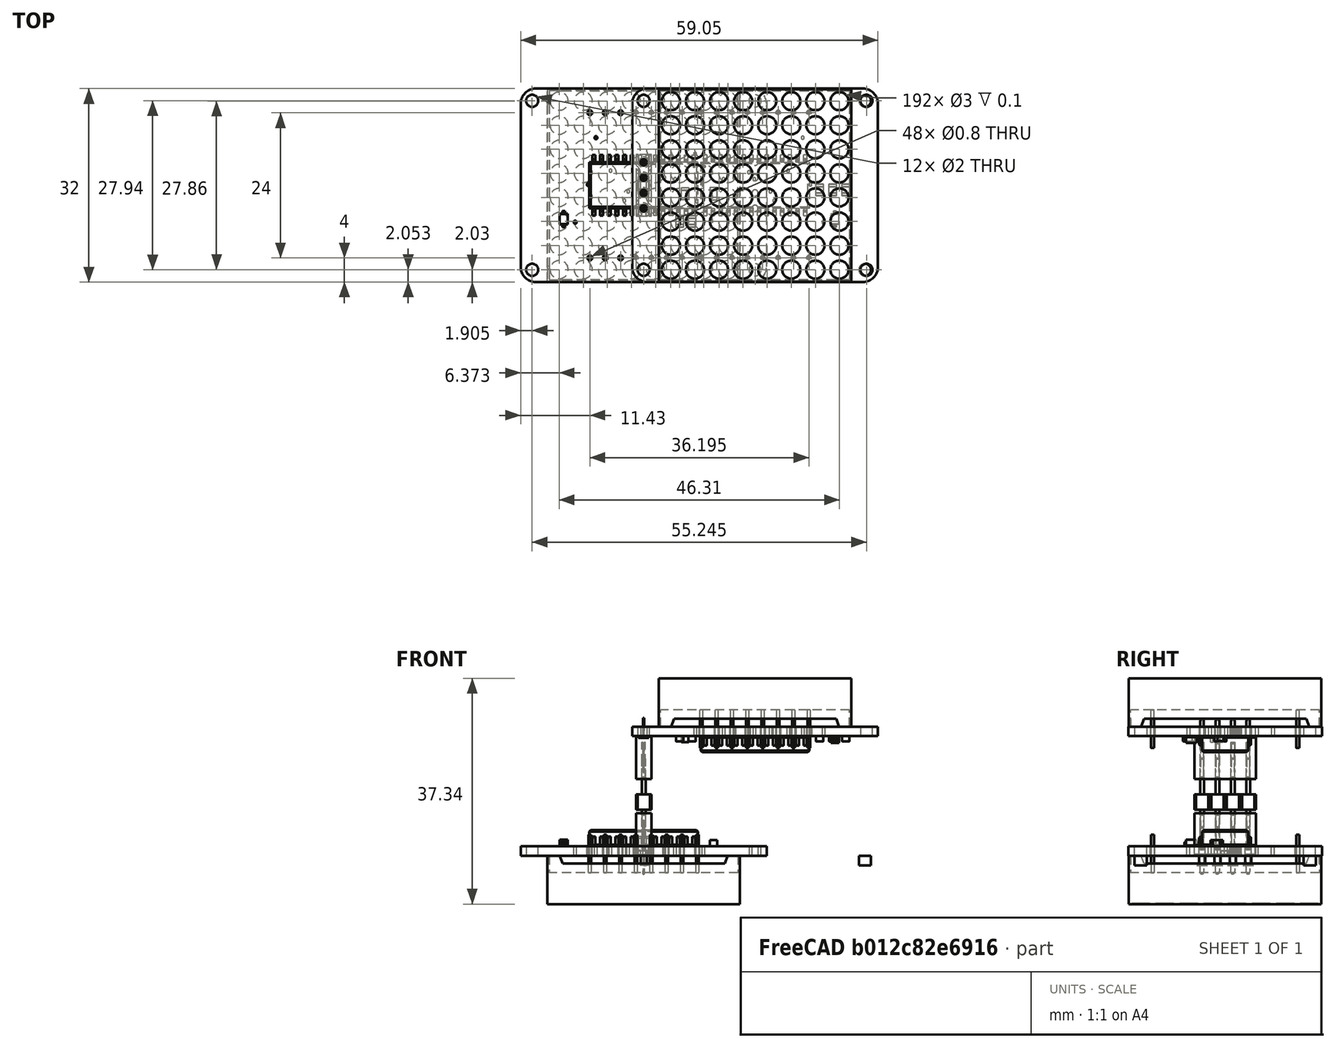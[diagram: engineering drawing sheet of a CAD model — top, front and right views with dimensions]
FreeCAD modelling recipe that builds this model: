
FCSTD DOCUMENT  (FreeCAD 2022.709R28846 (Git))
Label: footprint_LED_matrix_8x8_socket_v2
License: Other
objects: Part::Feature×33, Part::Compound×4, App::Link×4, App::Part×2, Path::FeatureArea×1, Part::Extrusion×1, App::DocumentObjectGroup×1, Part::Compound2×1, Part::MultiFuse×1
note: 41 computed .brp shape members not serialized (recipe doc carries the construction recipe); baked Part::Feature solids carry a one-line shape summary decoded from their .brp

FEATURE [Part::Feature] holes_wire  label="holes_wire#F.Cu#0"
  TreeRank = 3
  shape: bbox 38.08 x 29.94 x 2e-07 mm, 0 faces, 0 solids (baked)
FEATURE [Path::FeatureArea] holes_area  label="holes_area#F.Cu#0"
  Accuracy = 0.0005
  Angle = 45
  AngleShift = 0
  CleanDistance = 0
  ClipFill = 0
  ClipperScale = 10000000
  Coplanar = 0
  Deflection = 0.01
  EndType = 0
  Explode = false
  ExtraPass = 0
  Fill = 1
  FitArcs = true
  FromCenter = false
  JoinType = 0
  LastStepover = 0
  MaxArcPoints = 100
  MinArcPoints = 4
  MiterLimit = 2
  OpenMode = 0
  Operation = 0
  Outline = false
  PocketExtraOffset = 0
  PocketLastStepover = 0
  PocketMaxOffset = 0
  PocketMode = 0
  PocketStepover = 0
  Project = false
  Reorient = false
  RoundPrecision = 0
  SectionCount = 0
  SectionMode = 2
  SectionOffset = 0
  SectionTolerance = 1e-06
  Shift = 0
  Simplify = false
  Sources = -> [holes_wire]
  Stepdown = 1
  Stepover = 0
  SubjectFill = 0
  Thicken = false
  Tolerance = 1e-07
  ToolRadius = 1
  TreeRank = 4
  Unit = 1
FEATURE [Part::Extrusion] holes_solid  label="holes_solid#F.Cu"
  Base = -> holes_area
  Dir = (0,0,1.6)
  DirMode = 0
  FaceMakerClass = Part::FaceMakerBullseye
  InnerTaperAngle = 0
  InnerTaperAngleRev = 0
  LengthFwd = 0
  LengthRev = 0
  Linearize = true
  Placement = pos=(0,0,-1.6) rot=(0,0,1;0rad)
  Solid = false
  Symmetric = false
  TreeRank = 5
FEATURE [Part::Feature] anr_  label="drill_000"
  TreeRank = 37
  shape: bbox 2.02 x 2.02 x 1.6 mm, 4 faces (baked)
FEATURE [Part::Feature] anr_001  label="drill_001"
  TreeRank = 38
  shape: bbox 2.02 x 2.02 x 1.6 mm, 4 faces (baked)
FEATURE [Part::Feature] anr_002  label="drill_002"
  TreeRank = 39
  shape: bbox 1.02 x 1.02 x 1.6 mm, 4 faces (baked)
FEATURE [Part::Feature] anr_003  label="drill_003"
  TreeRank = 40
  shape: bbox 1.02 x 1.02 x 1.6 mm, 4 faces (baked)
FEATURE [Part::Feature] anr_004  label="drill_004"
  TreeRank = 41
  shape: bbox 1.02 x 1.02 x 1.6 mm, 4 faces (baked)
FEATURE [Part::Feature] anr_005  label="drill_005"
  TreeRank = 42
  shape: bbox 1.02 x 1.02 x 1.6 mm, 4 faces (baked)
FEATURE [Part::Compound] annulars  label="TH-Drills"
  Links = -> [anr_,anr_001,anr_002,anr_003,anr_004,anr_005]
  TreeRank = 43
FEATURE [Part::Feature] Shape001  label="topPads"
  Placement = pos=(0,0,-0.01) rot=(0,0,1;0rad)
  TreeRank = 52
  shape: bbox 1.8 x 9.42 x 0.01 mm, 20 faces, 4 solids (baked)
FEATURE [Part::Feature] Shape002  label="btmPads"
  Placement = pos=(0,0,-1.6) rot=(0,0,1;0rad)
  TreeRank = 58
  shape: bbox 1.8 x 9.42 x 0.01 mm, 20 faces, 4 solids (baked)
FEATURE [App::DocumentObjectGroup] Group  label=""LED_8x8_Bi_Color"-fp"
  ClaimAllChildren = true
  ExportMode = 1
  Group = -> [Shape001,Shape002,annulars]
  TreeRank = 59
  _GroupVersion = 1
FEATURE [Part::Feature] Solid  label="PinSocket_1x04_P254mm_Vertical"
  Placement = pos=(0,3.81,0) rot=(0,0,1;0rad)
  TreeRank = 60
  shape: bbox 2.54 x 10.16 x 10.1 mm, 134 faces (baked)
FEATURE [Part::Feature] Solid001  label="PinSocket_1x04_P254mm_Vertical001"
  Placement = pos=(0,-3.81,19.685) rot=(1,0,0;3.14159rad)
  TreeRank = 61
  shape: bbox 2.54 x 10.16 x 10.1 mm, 134 faces (baked)
FEATURE [Part::Feature] Solid002  label="PinHeader_1x04_P254mm_Vertical"
  Placement = pos=(0,3.81,7.62) rot=(0,0,1;0rad)
  TreeRank = 62
  shape: bbox 2.54 x 10.16 x 11.54 mm, 100 faces (baked)
FEATURE [Part::Feature] Solid003  label="Board"
  TreeRank = 65
  shape: bbox 40.64 x 32 x 1.57 mm, 45 faces (baked)
FEATURE [Part::Feature] Solid004  label="SEGMENT_BL-M12A881UR"
  Placement = pos=(0,0,0) rot=(0,1,0;3.14159rad)
  TreeRank = 66
  shape: bbox 31.8 x 31.8 x 11.5 mm, 186 faces (baked)
FEATURE [Part::Feature] Solid005
  TreeRank = 71
  shape: bbox 1.94 x 1.19 x 0.79 mm, 6 faces (baked)
FEATURE [Part::Feature] Solid006
  TreeRank = 72
  shape: bbox 0.5 x 1.25 x 0.85 mm, 30 faces (baked)
FEATURE [Part::Feature] Solid007
  TreeRank = 73
  shape: bbox 0.5 x 1.25 x 0.85 mm, 30 faces (baked)
FEATURE [Part::Compound2] Compound  label="R0805"
  Links = -> [Solid005,Solid006,Solid007]
  Placement = pos=(10.414,-5.969,1.57) rot=(0,0,-1;1.5708rad)
  TreeRank = 74
FEATURE [App::Link] Link  label="R0805:R2"
  AutoLinkLabel = true
  AutoPlacement = true
  LinkPlacement = pos=(12.446,-5.969,1.57) rot=(0,0,-1;1.5708rad)
  LinkedObject = -> Compound
  Placement = pos=(12.446,-5.969,1.57) rot=(0,0,-1;1.5708rad)
  ShowElement = false
  SyncGroupVisibility = false
  TreeRank = 86
  _LinkVersion = 1
FEATURE [App::Link] Link001  label="R0805:R3"
  AutoLinkLabel = true
  AutoPlacement = true
  LinkPlacement = pos=(-12.827,-0.762,1.57) rot=(0,0,1;1.5708rad)
  LinkedObject = -> Compound
  Placement = pos=(-12.827,-0.762,1.57) rot=(0,0,1;1.5708rad)
  ShowElement = false
  SyncGroupVisibility = false
  TreeRank = 87
  _LinkVersion = 1
FEATURE [App::Link] Link002  label="R0805:R4"
  AutoLinkLabel = true
  AutoPlacement = true
  LinkPlacement = pos=(-10.668,-0.762,1.57) rot=(0,0,1;1.5708rad)
  LinkedObject = -> Compound
  Placement = pos=(-10.668,-0.762,1.57) rot=(0,0,1;1.5708rad)
  ShowElement = false
  SyncGroupVisibility = false
  TreeRank = 88
  _LinkVersion = 1
FEATURE [App::Link] Link003  label="R0805:R5"
  AutoLinkLabel = true
  AutoPlacement = true
  LinkPlacement = pos=(-14.986,-0.762,1.57) rot=(0,0,1;1.5708rad)
  LinkedObject = -> Compound
  Placement = pos=(-14.986,-0.762,1.57) rot=(0,0,1;1.5708rad)
  ShowElement = false
  SyncGroupVisibility = false
  TreeRank = 89
  _LinkVersion = 1
FEATURE [Part::Feature] Solid008  label="SOD-323F"
  Placement = pos=(-13.208,-5.588,1.57) rot=(0,0,1;1.5708rad)
  TreeRank = 90
  shape: bbox 1.35 x 2.7 x 1.1 mm, 38 faces (baked)
FEATURE [Part::Feature] Solid009  label="C0805"
  Placement = pos=(11.557,-1.397,1.57) rot=(0,0,1;1.5708rad)
  TreeRank = 91
  shape: bbox 1.25 x 2 x 1 mm, 14 faces (baked)
FEATURE [Part::Feature] Solid010  label="SOP28_300MIL"
  Placement = pos=(0,0,1.57) rot=(0,0,1;3.14159rad)
  TreeRank = 92
  shape: bbox 18 x 10 x 2.65 mm, 376 faces (baked)
FEATURE [App::Part] Part  label="PCB Component"
  ClaimAllChildren = false
  ExportMode = 1
  Group = -> [Solid003,Solid004,Compound,Link,Link001,Link002,Link003,Solid008,Solid009,Solid010,Solid005,Solid006,Solid007]
  Origin = -> Origin
  TreeRank = 94
  _ExportChildren = -> [Solid003,Solid004,Compound,Link,Link001,Link002,Link003,Solid008,Solid009,Solid010]
  _GroupVersion = 1
FEATURE [App::Part] Part001  label="Adafruit 1.2inch 8x8 backpack v2"
  ClaimAllChildren = false
  ExportMode = 1
  Group = -> [Part]
  Origin = -> Origin001
  Placement = pos=(18.415,2.7e-15,21.336) rot=(0,1,0;3.14159rad)
  TreeRank = 96
  _ExportChildren = -> [Part]
  _GroupVersion = 1
FEATURE [Part::Compound] PinSocket_1x04_P254mm_Vertical_mp
  Links = -> [Solid,Solid001,Solid002]
  TreeRank = 97
FEATURE [Part::Feature] PinSocket_1x04_P254mm_Vertical_mp_cp  label="PinSocket_1x04_P254mm_Vertical_sp"
  TreeRank = 98
  shape: bbox 2.54 x 10.16 x 25.89 mm, 368 faces, 3 solids (baked)
FEATURE [Part::Feature] Solid003_cp  label="Board_cp"
  TreeRank = 110
  shape: bbox 40.64 x 32 x 1.57 mm, 45 faces (baked)
FEATURE [Part::Feature] Solid004_cp  label="SEGMENT_BL-M12A881UR_cp"
  Placement = pos=(0,0,0) rot=(0,1,0;3.14159rad)
  TreeRank = 111
  shape: bbox 31.8 x 31.8 x 11.5 mm, 186 faces (baked)
FEATURE [Part::Feature] LinkGroup  label="R0806"
  Placement = pos=(10.414,-5.969,1.57) rot=(0,0,-1;1.5708rad)
  TreeRank = 112
  shape: bbox 1.25 x 2 x 0.85 mm, 66 faces, 3 solids (baked)
FEATURE [Part::Feature] Link_cp  label="R0805:R2_cp"
  Placement = pos=(12.446,-5.969,1.57) rot=(0,0,-1;1.5708rad)
  TreeRank = 113
  shape: bbox 1.25 x 2 x 0.85 mm, 66 faces, 3 solids (baked)
FEATURE [Part::Feature] Link001_cp  label="R0805:R3_cp"
  Placement = pos=(-12.827,-0.762,1.57) rot=(0,0,1;1.5708rad)
  TreeRank = 114
  shape: bbox 1.25 x 2 x 0.85 mm, 66 faces, 3 solids (baked)
FEATURE [Part::Feature] Link002_cp  label="R0805:R4_cp"
  Placement = pos=(-10.668,-0.762,1.57) rot=(0,0,1;1.5708rad)
  TreeRank = 115
  shape: bbox 1.25 x 2 x 0.85 mm, 66 faces, 3 solids (baked)
FEATURE [Part::Feature] Link003_cp  label="R0805:R5_cp"
  Placement = pos=(-14.986,-0.762,1.57) rot=(0,0,1;1.5708rad)
  TreeRank = 116
  shape: bbox 1.25 x 2 x 0.85 mm, 66 faces, 3 solids (baked)
FEATURE [Part::Feature] Solid008_cp  label="SOD-323F_cp"
  Placement = pos=(-13.208,-5.588,1.57) rot=(0,0,1;1.5708rad)
  TreeRank = 117
  shape: bbox 1.35 x 2.7 x 1.1 mm, 38 faces (baked)
FEATURE [Part::Feature] Solid009_cp  label="C0805_cp"
  Placement = pos=(11.557,-1.397,1.57) rot=(0,0,1;1.5708rad)
  TreeRank = 118
  shape: bbox 1.25 x 2 x 1 mm, 14 faces (baked)
FEATURE [Part::Feature] Solid010_cp  label="SOP28_300MIL_cp"
  Placement = pos=(0,0,1.57) rot=(0,0,1;3.14159rad)
  TreeRank = 119
  shape: bbox 18 x 10 x 2.65 mm, 376 faces (baked)
FEATURE [Part::Compound] Adafruit_1_2inch_8x8_backpack_v2_cp
  Links = -> [Solid003_cp,Solid004_cp,LinkGroup,Link_cp,Link001_cp,Link002_cp,Link003_cp,Solid008_cp,Solid009_cp,Solid010_cp]
  Placement = pos=(18.415,2.7e-15,21.336) rot=(0,1,0;3.14159rad)
  TreeRank = 120
FEATURE [Part::MultiFuse] Adafruit_1_2inch_8x8_backpack_v2_mp_cp  label="Adafruit 1.2inch 8x8 backpack v2_fd"
  Shapes = -> [Adafruit_1_2inch_8x8_backpack_v2_cp]
  TreeRank = 121
FEATURE [Part::Feature] Adafruit_1_2inch_8x8_backpack_v2_fd_cp  label="Adafruit 1.2inch 8x8 backpack v2_sp"
  TreeRank = 122
  shape: bbox 40.64 x 32 x 12.22 mm, 884 faces (baked)
FEATURE [Part::Compound] PinSocket_1x04_P254mm_Vertical_sp_mp
  Links = -> [PinSocket_1x04_P254mm_Vertical_mp_cp,Adafruit_1_2inch_8x8_backpack_v2_fd_cp]
  TreeRank = 123
FEATURE [Part::Feature] PinSocket_1x04_P254mm_Vertical_sp_mp_cp  label="LED_matrix_8x8_socket"
  TreeRank = 124
  shape: bbox 40.64 x 32 x 32.44 mm, 1252 faces, 4 solids (baked)
